# Revit family: Accessory-Robe_Hook-KOHLER-LOURE-K-11585T_1
name_source: partatom
category: Specialty Equipment
revit_build: Autodesk Revit 2017 (Build: 20160225_1515(x64)
units: mm (PartAtom-declared; Revit-internal decimal feet)

## family parameters
Cut with Voids When Loaded = No
Host = Face
OmniClass Number = 23.31.25.27
OmniClass Title = Robe Hooks
Part Type = Normal
Room Calculation Point = No
Round Connector Dimension = Use Diameter
Shared = No

## types (2) — shared parameters
ADA Compliant = No
Assembly Code = C1030200
Date Modified = 06/15/2020
Default Elevation = 42"
Description = Hook/Hanger
Height = 2 1/2"
Length = 2 3/4"
Manufacturer = KOHLER Co.
Master Format 2014 = 10 28 00
Master Format 2014 Name = Toilet, Bath, and Laundry Accessories
Material = Solid Metal Construction
Product Documentation Link = http://files.kohler.com.cn
Product Name = LOURE
Product Page URL = http://m.kohler.com.cn
URL = http://www.kohler.com.cn
WaterSense Certified = No
Width = 12"

## per-type parameters (varying)
| type | Finish | Model | Type |
| CP-Polished Chrome | Kohler-Metal-CP-Polished_Chrome | K-11585T-CP | 1 |
| 2BL-Original Black | Kohler-Metal-2BL-Original_Black | K-11585T-2BL | 2 |

## geometry (parser evidence)
native form markers: Sweep x3
no freeform markers — native parametric forms only
